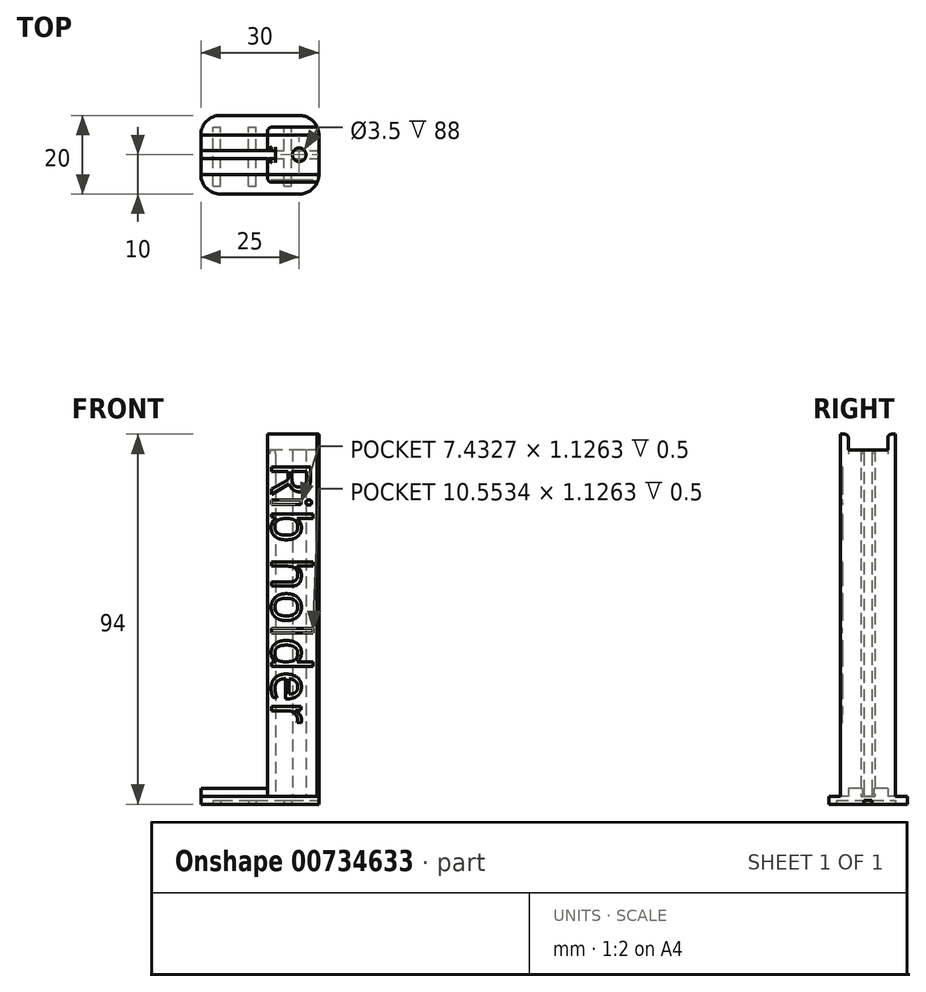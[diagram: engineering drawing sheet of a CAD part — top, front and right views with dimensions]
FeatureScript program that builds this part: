
annotation { "Feature Type Name" : "Feature", "Feature Type Description" : "" }
export const myFeature = defineFeature(function(context is Context, id is Id, definition is map)
    precondition{}
    {
        {
            var Q0;
            Q0=qCreatedBy(makeId("Top.planeOp"),FACE);
            var sketch = newSketch(context, id + "F0", { "sketchPlane" : qUnion([Q0])});
            skLineSegment(sketch, "E0.bottom", {"start": v(-5, 10) * mm, "end": v(-25, 10) * mm});
            skLineSegment(sketch, "E0.top", {"start": v(-5, -10) * mm, "end": v(-25, -10) * mm});
            skLineSegment(sketch, "E0.left", {"start": v(0, 5) * mm, "end": v(0, -5) * mm});
            skLineSegment(sketch, "E0.right", {"start": v(-30, 5) * mm, "end": v(-30, -5) * mm});
            skPoint(sketch, "E1.visualSharp", {"position": v(-30, 10) * mm});
            skArc(sketch, "E1.filletArc", {"start": v(-25, 10) * mm, "mid": v(-28.54, 8.54) * mm, "end": v(-30, 5) * mm});
            skPoint(sketch, "E2.visualSharp", {"position": v(-30, -10) * mm});
            skArc(sketch, "E2.filletArc", {"start": v(-30, -5) * mm, "mid": v(-28.54, -8.54) * mm, "end": v(-25, -10) * mm});
            skPoint(sketch, "E3.visualSharp", {"position": v(0, -10) * mm});
            skArc(sketch, "E3.filletArc", {"start": v(-5, -10) * mm, "mid": v(-1.46, -8.54) * mm, "end": v(0, -5) * mm});
            skPoint(sketch, "E4.visualSharp", {"position": v(0, 10) * mm});
            skArc(sketch, "E4.filletArc", {"start": v(0, 5) * mm, "mid": v(-1.46, 8.54) * mm, "end": v(-5, 10) * mm});
            skSolve(sketch);
        }
        {
            var Q0;
            Q0 = qSketchRegion(id + "F0", true);
            extrude(context, id + "F1", {"entities" : qUnion([Q0]), "depth" : 2 * mm, "offsetDistance" : 25 * mm});
        }
        {
            var Q0;
            Q0=makeQuery(id+"F1.opExtrude","CAP_FACE",FACE,{"disambiguationData":[OSD([sQuery(id+"F0.wireOp",EDGE,"E0.bottom"),sQuery(id+"F0.wireOp",EDGE,"E0.top"),sQuery(id+"F0.wireOp",EDGE,"E0.left"),sQuery(id+"F0.wireOp",EDGE,"E0.right"),sQuery(id+"F0.wireOp",EDGE,"E1.filletArc"),sQuery(id+"F0.wireOp",EDGE,"E2.filletArc"),sQuery(id+"F0.wireOp",EDGE,"E3.filletArc"),sQuery(id+"F0.wireOp",EDGE,"E4.filletArc")])],"isStart":false});
            var sketch = newSketch(context, id + "F2", { "sketchPlane" : qUnion([Q0])});
            skLineSegment(sketch, "E5.bottom", {"start": v(0, 5) * mm, "end": v(-13, 5) * mm});
            skLineSegment(sketch, "E5.top", {"start": v(0, -5) * mm, "end": v(-13, -5) * mm});
            skLineSegment(sketch, "E5.left", {"start": v(0, 5) * mm, "end": v(0, -5) * mm});
            skLineSegment(sketch, "E5.right", {"start": v(-13, 5) * mm, "end": v(-13, 1.5) * mm});
            skLineSegment(sketch, "E6.bottom", {"start": v(-12.5, 1) * mm, "end": v(-11, 1) * mm});
            skLineSegment(sketch, "E6.top", {"start": v(-12.5, -1) * mm, "end": v(-11, -1) * mm});
            skLineSegment(sketch, "E6.right", {"start": v(-11, 1) * mm, "end": v(-11, -1) * mm});
            skLineSegment(sketch, "E7.trimOffspring", {"start": v(-13, -1.5) * mm, "end": v(-13, -5) * mm});
            skPoint(sketch, "E8.visualSharp", {"position": v(-13, 1) * mm});
            skArc(sketch, "E8.filletArc", {"start": v(-13, 1.5) * mm, "mid": v(-12.85, 1.15) * mm, "end": v(-12.5, 1) * mm});
            skPoint(sketch, "E9.visualSharp", {"position": v(-13, -1) * mm});
            skArc(sketch, "E9.filletArc", {"start": v(-12.5, -1) * mm, "mid": v(-12.85, -1.15) * mm, "end": v(-13, -1.5) * mm});
            skCircle(sketch, "E10", {"center": v(-5, 0) * mm, "radius": 1.75 * mm});
            skSolve(sketch);
        }
        {
            var Q0;
            Q0 = qSketchRegion(id + "F2", true);
            extrude(context, id + "F3", {"entities" : qUnion([Q0]), "operationType" : NewBodyOperationType.ADD, "depth" : 88 * mm, "offsetDistance" : 25 * mm});
        }
        {
            var Q0;
            Q0=makeQuery(id+"F1.opExtrude","CAP_FACE",FACE,{"disambiguationData":[OSD([sQuery(id+"F0.wireOp",EDGE,"E0.bottom"),sQuery(id+"F0.wireOp",EDGE,"E0.top"),sQuery(id+"F0.wireOp",EDGE,"E0.left"),sQuery(id+"F0.wireOp",EDGE,"E0.right"),sQuery(id+"F0.wireOp",EDGE,"E1.filletArc"),sQuery(id+"F0.wireOp",EDGE,"E2.filletArc"),sQuery(id+"F0.wireOp",EDGE,"E3.filletArc"),sQuery(id+"F0.wireOp",EDGE,"E4.filletArc")])],"isStart":true});
            var sketch = newSketch(context, id + "F4", { "sketchPlane" : qUnion([Q0])});
            skLineSegment(sketch, "E11.bottom", {"start": v(-24.92, 1) * mm, "end": v(-17.92, 1) * mm});
            skLineSegment(sketch, "E11.top", {"start": v(-24.92, -1) * mm, "end": v(-17.92, -1) * mm});
            skLineSegment(sketch, "E11.left", {"start": v(-26.92, 1) * mm, "end": v(-26.92, -1) * mm});
            skLineSegment(sketch, "E11.right", {"start": v(0, 1) * mm, "end": v(0, -1) * mm});
            skLineSegment(sketch, "E12.bottom", {"start": v(-26.92, 8) * mm, "end": v(-24.92, 8) * mm});
            skLineSegment(sketch, "E12.top", {"start": v(-26.92, -7) * mm, "end": v(-24.92, -7) * mm});
            skLineSegment(sketch, "E12.left", {"start": v(-26.92, 8) * mm, "end": v(-26.92, 1) * mm});
            skLineSegment(sketch, "E12.right", {"start": v(-24.92, 8) * mm, "end": v(-24.92, 1) * mm});
            skLineSegment(sketch, "E13.trimOffspring", {"start": v(-24.92, -1) * mm, "end": v(-24.92, -7) * mm});
            skLineSegment(sketch, "E14.trimOffspring", {"start": v(-26.92, -1) * mm, "end": v(-26.92, -7) * mm});
            skLineSegment(sketch, "E15.bottom", {"start": v(-17.92, 8) * mm, "end": v(-15.92, 8) * mm});
            skLineSegment(sketch, "E15.top", {"start": v(-17.92, -7) * mm, "end": v(-15.92, -7) * mm});
            skLineSegment(sketch, "E15.left", {"start": v(-17.92, 8) * mm, "end": v(-17.92, 1) * mm});
            skLineSegment(sketch, "E15.right", {"start": v(-15.92, 8) * mm, "end": v(-15.92, 1) * mm});
            skLineSegment(sketch, "E16.trimOffspring", {"start": v(-15.92, -1) * mm, "end": v(-15.92, -7) * mm});
            skLineSegment(sketch, "E17.trimOffspring", {"start": v(-17.92, -1) * mm, "end": v(-17.92, -7) * mm});
            skLineSegment(sketch, "E18.trimOffspring", {"start": v(-15.92, -1) * mm, "end": v(-8.92, -1) * mm});
            skLineSegment(sketch, "E19.trimOffspring", {"start": v(-15.92, 1) * mm, "end": v(-8.92, 1) * mm});
            skLineSegment(sketch, "E20.bottom", {"start": v(-8.92, 8) * mm, "end": v(-6.92, 8) * mm});
            skLineSegment(sketch, "E20.top", {"start": v(-8.92, -7) * mm, "end": v(-6.92, -7) * mm});
            skLineSegment(sketch, "E20.left", {"start": v(-8.92, 8) * mm, "end": v(-8.92, 1) * mm});
            skLineSegment(sketch, "E20.right", {"start": v(-6.92, 8) * mm, "end": v(-6.92, 1) * mm});
            skLineSegment(sketch, "E21.trimOffspring", {"start": v(-6.92, -1) * mm, "end": v(-6.92, -7) * mm});
            skLineSegment(sketch, "E22.trimOffspring", {"start": v(-8.92, -1) * mm, "end": v(-8.92, -7) * mm});
            skLineSegment(sketch, "E23.trimOffspring", {"start": v(-6.92, 1) * mm, "end": v(0, 1) * mm});
            skLineSegment(sketch, "E24.trimOffspring", {"start": v(-6.92, -1) * mm, "end": v(0, -1) * mm});
            skSolve(sketch);
        }
        {
            var Q0;
            Q0 = qSketchRegion(id + "F4", true);
            extrude(context, id + "F5", {"entities" : qUnion([Q0]), "operationType" : NewBodyOperationType.REMOVE, "oppositeDirection" : true, "depth" : 1 * mm, "offsetDistance" : 25 * mm});
        }
        {
            var Q0;
            {var subQ0=sQuery(id+"F0.wireOp",EDGE,"E0.left");var subQ1=sQuery(id+"F0.wireOp",EDGE,"E4.filletArc");var subQ2=sQuery(id+"F0.wireOp",EDGE,"E3.filletArc");var subQ3=sQuery(id+"F0.wireOp",EDGE,"E2.filletArc");var subQ4=sQuery(id+"F0.wireOp",EDGE,"E1.filletArc");var subQ5=sQuery(id+"F0.wireOp",EDGE,"E0.bottom");var subQ6=sQuery(id+"F0.wireOp",EDGE,"E0.right");var subQ7=sQuery(id+"F0.wireOp",EDGE,"E0.top");Q0=makeQuery(id+"F3.boolean.opBoolean","SPLIT",FACE,{"disambiguationData":[TD([makeQuery(id+"F1.opExtrude","SWEPT_FACE",FACE,{"disambiguationData":[OSD([subQ5])]})])],"derivedFrom":makeQuery(id+"F1.opExtrude","CAP_FACE",FACE,{"disambiguationData":[OSD([subQ5,subQ7,subQ0,subQ6,subQ4,subQ3,subQ2,subQ1])],"isStart":false})});}
            var sketch = newSketch(context, id + "F6", { "sketchPlane" : qUnion([Q0])});
            skLineSegment(sketch, "E25.bottom", {"start": v(-13, 5) * mm, "end": v(0, 5) * mm});
            skLineSegment(sketch, "E25.top", {"start": v(-13, 7) * mm, "end": v(-0.42, 7) * mm});
            skLineSegment(sketch, "E25.left", {"start": v(-13, 5) * mm, "end": v(-13, 7) * mm});
            skArc(sketch, "E26.0", {"start": v(0, 5) * mm, "mid": v(-0.1, 6.02) * mm, "end": v(-0.42, 7) * mm});
            skPoint(sketch, "E25.right.end.orphan", {"position": v(0, 7) * mm});
            skPoint(sketch, "E27.MirrorP", {"position": v(0, -7) * mm});
            skLineSegment(sketch, "E28.MirrorCS", {"start": v(-13, -5) * mm, "end": v(0, -5) * mm});
            skArc(sketch, "E29.MirrorCS", {"start": v(0, -5) * mm, "mid": v(-0.1, -6.02) * mm, "end": v(-0.42, -7) * mm});
            skLineSegment(sketch, "E30.MirrorCS", {"start": v(-13, -5) * mm, "end": v(-13, -7) * mm});
            skLineSegment(sketch, "E31.MirrorCS", {"start": v(-13, -7) * mm, "end": v(-0.42, -7) * mm});
            skSolve(sketch);
        }
        {
            var Q0;
            Q0 = qSketchRegion(id + "F6", true);
            extrude(context, id + "F7", {"entities" : qUnion([Q0]), "operationType" : NewBodyOperationType.ADD, "depth" : 92 * mm, "offsetDistance" : 25 * mm});
        }
        {
            var Q0;
            Q0=makeQuery(id+"F7.opExtrude","SWEPT_FACE",FACE,{"disambiguationData":[OSD([sQuery(id+"F6.wireOp",EDGE,"E31.MirrorCS")])]});
            var sketch = newSketch(context, id + "F8", { "sketchPlane" : qUnion([Q0])});
            skText(sketch, "E32", { "text": "Rib holder", "fontName": "OpenSans-Regular.ttf"});
            const initialGuessF8  = {"E32": [-0.012, 0.087, 0, -1, 0.01]};
            skSetInitialGuess(sketch, initialGuessF8);
            skSolve(sketch);
        }
        {
            var Q0;
            Q0 = qSketchRegion(id + "F8", true);
            extrude(context, id + "F9", {"entities" : qUnion([Q0]), "operationType" : NewBodyOperationType.REMOVE, "oppositeDirection" : true, "depth" : 0.5 * mm, "offsetDistance" : 25 * mm});
        }
        {
            var Q0;
            Q0=makeQuery(id+"F7.opExtrude","SWEPT_EDGE",EDGE,{"disambiguationData":[OSD([sQuery(id+"F6.wireOp",EDGE,"E25.top"),sQuery(id+"F6.wireOp",EDGE,"E25.left")])]});
            var Q1;
            Q1=makeQuery(id+"F7.opExtrude","SWEPT_EDGE",EDGE,{"disambiguationData":[OSD([sQuery(id+"F6.wireOp",EDGE,"E30.MirrorCS"),sQuery(id+"F6.wireOp",EDGE,"E31.MirrorCS")])]});
            fillet(context, id + "F10", {"entities" : qUnion([Q0, Q1]), "tangentPropagation" : true, "radius" : 1 * mm, "defaultsChanged" : false, "vertexSettings" : [], "allowEdgeOverflow" : false});
        }
        {
            var Q0;
            {var subQ0=sQuery(id+"F0.wireOp",EDGE,"E0.left");var subQ1=sQuery(id+"F0.wireOp",EDGE,"E4.filletArc");var subQ2=sQuery(id+"F0.wireOp",EDGE,"E3.filletArc");var subQ3=sQuery(id+"F0.wireOp",EDGE,"E2.filletArc");var subQ4=sQuery(id+"F0.wireOp",EDGE,"E1.filletArc");var subQ5=sQuery(id+"F0.wireOp",EDGE,"E0.bottom");var subQ6=sQuery(id+"F0.wireOp",EDGE,"E0.right");var subQ7=sQuery(id+"F0.wireOp",EDGE,"E0.top");Q0=makeQuery(id+"F3.boolean.opBoolean","SPLIT",FACE,{"disambiguationData":[TD([makeQuery(id+"F1.opExtrude","SWEPT_FACE",FACE,{"disambiguationData":[OSD([subQ5])]})])],"derivedFrom":makeQuery(id+"F1.opExtrude","CAP_FACE",FACE,{"disambiguationData":[OSD([subQ5,subQ7,subQ0,subQ6,subQ4,subQ3,subQ2,subQ1])],"isStart":false})});}
            var sketch = newSketch(context, id + "F11", { "sketchPlane" : qUnion([Q0])});
            skLineSegment(sketch, "E33.bottom", {"start": v(-30, 5) * mm, "end": v(-13, 5) * mm});
            skLineSegment(sketch, "E33.top", {"start": v(-30, -5) * mm, "end": v(-13, -5) * mm});
            skLineSegment(sketch, "E33.left", {"start": v(-30, 5) * mm, "end": v(-30, 1) * mm});
            skLineSegment(sketch, "E33.right", {"start": v(-13, 5) * mm, "end": v(-13, 1) * mm});
            skLineSegment(sketch, "E34.bottom", {"start": v(-30, 1) * mm, "end": v(-13, 1) * mm});
            skLineSegment(sketch, "E34.top", {"start": v(-30, -1) * mm, "end": v(-13, -1) * mm});
            skLineSegment(sketch, "E35.trimOffspring", {"start": v(-30, -1) * mm, "end": v(-30, -5) * mm});
            skLineSegment(sketch, "E36.trimOffspring", {"start": v(-13, -1) * mm, "end": v(-13, -5) * mm});
            skSolve(sketch);
        }
        {
            var Q0;
            Q0 = qSketchRegion(id + "F11", true);
            extrude(context, id + "F12", {"entities" : qUnion([Q0]), "operationType" : NewBodyOperationType.ADD, "depth" : 2 * mm, "offsetDistance" : 25 * mm});
        }
        {
            var Q0;
            Q0=makeQuery(id+"F12.opExtrude","CAP_EDGE",EDGE,{"disambiguationData":[OSD([sQuery(id+"F11.wireOp",EDGE,"E34.top")])],"isStart":false});
            var Q1;
            Q1=makeQuery(id+"F12.opExtrude","CAP_EDGE",EDGE,{"disambiguationData":[OSD([sQuery(id+"F11.wireOp",EDGE,"E34.bottom")])],"isStart":false});
            var Q2;
            Q2=makeQuery(id+"F3.opExtrude","CAP_EDGE",EDGE,{"disambiguationData":[OSD([sQuery(id+"F2.wireOp",EDGE,"E6.bottom")])],"isStart":false});
            var Q3;
            Q3=makeQuery(id+"F3.opExtrude","CAP_EDGE",EDGE,{"disambiguationData":[OSD([sQuery(id+"F2.wireOp",EDGE,"E6.top")])],"isStart":false});
            var Q4;
            Q4=makeQuery(id+"F7.opExtrude","CAP_EDGE",EDGE,{"disambiguationData":[OSD([sQuery(id+"F6.wireOp",EDGE,"E25.bottom")])],"isStart":false});
            var Q5;
            Q5=makeQuery(id+"F7.opExtrude","CAP_EDGE",EDGE,{"disambiguationData":[OSD([sQuery(id+"F6.wireOp",EDGE,"E28.MirrorCS")])],"isStart":false});
            fillet(context, id + "F13", {"entities" : qUnion([Q0, Q1, Q2, Q3, Q4, Q5]), "tangentPropagation" : true, "radius" : 1 * mm, "defaultsChanged" : false, "vertexSettings" : [], "allowEdgeOverflow" : false});
        }
    });
